FCSTD DOCUMENT  (FreeCAD 0.16R)
Label: CableGuide
License: All rights reserved
LicenseURL: http://en.wikipedia.org/wiki/All_rights_reserved
objects: Sketcher::SketchObject×7, PartDesign::Pocket×5, PartDesign::Pad×2, PartDesign::Mirrored×2, PartDesign::PolarPattern×1, Part::FeaturePython×1, Mesh::Feature×1
note: 25 computed .brp shape members not serialized (recipe doc carries the construction recipe); baked Part::Feature solids carry a one-line shape summary decoded from their .brp

FEATURE [Sketcher::SketchObject] Sketch
  sketch-geometry (1):
    g0: Circle CenterX=0 CenterY=0 CenterZ=0 NormalX=0 NormalY=0 NormalZ=1 Radius=14
  constraints (2):
    c: Coincident(g0,g-1)
    c: Radius(g0) = 14
FEATURE [PartDesign::Pad] Pad  label="ring"
  Length = 13
  Length2 = 100
  Sketch = -> Sketch
  Type = 0
FEATURE [Sketcher::SketchObject] Sketch001
  Placement = pos=(0,0,13) rot=(0,0,1;0rad)
  Support = -> Pad [Face3]
  sketch-geometry (1):
    g0: Circle CenterX=0 CenterY=0 CenterZ=0 NormalX=0 NormalY=0 NormalZ=1 Radius=11.1
  constraints (2):
    c: Coincident(g0,g-1)
    c: Radius(g0) = 11.1
FEATURE [PartDesign::Pocket] Pocket  label="STHole"
  Length = 5
  Sketch = -> Sketch001
  Type = 1
FEATURE [Sketcher::SketchObject] Sketch002
  Placement = pos=(0,0,13) rot=(0,0,1;0rad)
  Support = -> Pocket [Face3]
  sketch-geometry (4):
    g0: LineSegment StartX=-8.5 StartY=15.1 StartZ=0 EndX=8.5 EndY=15.1 EndZ=0
    g1: LineSegment StartX=8.5 StartY=15.1 StartZ=0 EndX=8.5 EndY=11.1 EndZ=0
    g2: LineSegment StartX=8.5 StartY=11.1 StartZ=0 EndX=-8.5 EndY=11.1 EndZ=0
    g3: LineSegment StartX=-8.5 StartY=11.1 StartZ=0 EndX=-8.5 EndY=15.1 EndZ=0
  constraints (12):
    c: Coincident(g0,g1)
    c: Coincident(g1,g2)
    c: Coincident(g2,g3)
    c: Coincident(g3,g0)
    c: Horizontal(g0)
    c: Horizontal(g2)
    c: Vertical(g1)
    c: Vertical(g3)
    c: Symmetric(g1,g2,g-2)
    c: Distance(g-1,g2) = 11.1
    c: Distance(g1) = 4
    c: Distance(g0) = 17
FEATURE [PartDesign::Pad] Pad001  label="boss"
  Length = 10
  Length2 = 100
  Reversed = true
  Sketch = -> Sketch002
  Type = 0
FEATURE [PartDesign::PolarPattern] PolarPattern
  Angle = 360
  Axis = -> Sketch002 [N_Axis]
  Occurrences = 2
  Originals = -> [Pad001]
FEATURE [Sketcher::SketchObject] Sketch003  label="cableHole"
  Placement = pos=(0,-10,0) rot=(1,0,0;1.5708rad)
  Support = -> PolarPattern [Face40]
  sketch-geometry (1):
    g0: Circle CenterX=12.1 CenterY=5 CenterZ=0 NormalX=0 NormalY=0 NormalZ=1 Radius=0.5
  constraints (3):
    c: DistanceY(g-1,g0) = 5
    c: DistanceX(g-1,g0) = 12.1
    c: Radius(g0) = 0.5
FEATURE [PartDesign::Pocket] Pocket001  label="CableHole"
  Length = 5
  Sketch = -> Sketch003
  Type = 1
FEATURE [PartDesign::Mirrored] Mirrored
  MirrorPlane = -> Sketch003 [V_Axis]
  Originals = -> [Pocket001]
FEATURE [Sketcher::SketchObject] Sketch004
  Placement = pos=(-10,0,0) rot=(-0.57735,0.57735,0.57735;4.18879rad)
  Support = -> Mirrored [Face53]
  sketch-geometry (1):
    g0: Circle CenterX=13.1 CenterY=5 CenterZ=0 NormalX=0 NormalY=0 NormalZ=1 Radius=1
  constraints (3):
    c: DistanceY(g-1,g0) = 5
    c: Radius(g0) = 1
    c: DistanceX(g-1,g0) = 13.1
FEATURE [PartDesign::Pocket] Pocket002  label="ScrewHole"
  Length = 5
  Sketch = -> Sketch004
  Type = 1
FEATURE [PartDesign::Mirrored] Mirrored001
  MirrorPlane = -> Sketch004 [V_Axis]
  Originals = -> [Pocket002]
FEATURE [Sketcher::SketchObject] Sketch005
  Placement = pos=(0,-15.1,0) rot=(1,0,0;1.5708rad)
  Support = -> PolarPattern [Face28]
  sketch-geometry (1):
    g0: Circle CenterX=0 CenterY=19 CenterZ=0 NormalX=0 NormalY=0 NormalZ=1 Radius=11.1
  constraints (3):
    c: DistanceY(g-1,g0) = 19
    c: DistanceX(g-2,g0) = 0
    c: Radius(g0) = 11.1
FEATURE [PartDesign::Pocket] Pocket003
  Length = 5
  Sketch = -> Sketch005
  Type = 1
FEATURE [Sketcher::SketchObject] Sketch006
  Placement = pos=(0,-15.1,0) rot=(1,0,0;1.5708rad)
  Support = -> Pocket003 [Face14]
  sketch-geometry (4):
    g0: LineSegment StartX=-0.5 StartY=9.58917 StartZ=0 EndX=0.5 EndY=9.58917 EndZ=0
    g1: LineSegment StartX=0.5 StartY=9.58917 StartZ=0 EndX=0.5 EndY=0 EndZ=0
    g2: LineSegment StartX=0.5 StartY=0 StartZ=0 EndX=-0.5 EndY=0 EndZ=0
    g3: LineSegment StartX=-0.5 StartY=0 StartZ=0 EndX=-0.5 EndY=9.58917 EndZ=0
  constraints (12):
    c: Coincident(g0,g1)
    c: Coincident(g1,g2)
    c: Coincident(g2,g3)
    c: Coincident(g3,g0)
    c: Horizontal(g0)
    c: Horizontal(g2)
    c: Vertical(g1)
    c: Vertical(g3)
    c: DistanceY(g-1,g1) = 0
    c: Symmetric(g1,g2,g-1)
    c: DistanceX(g0,g0) = 1
    c: DistanceY(g3,g3) = 9.58917
FEATURE [PartDesign::Pocket] Pocket004
  Length = 30
  Sketch = -> Sketch006
  Type = 0
FEATURE [Part::FeaturePython] refine  label="refine_Pocket004"  # WARN: FeaturePython — macro-defined, semantics opaque (R4)
  Base = -> Pocket004
FEATURE [Mesh::Feature] Mesh  label="refine_Pocket004 (Meshed)"
